FREECAD ASSEMBLY — COMPONENT RECIPES ("Machine")

This assembly document has 15 components, labeled P0..P14 below (a component is one placed body or linked part). 12 of them carry a construction recipe — the FreeCAD feature program that regenerates the part from scratch, quoted from this document or its linked companion documents; the rest are supplied as boundary geometry only. No exploded tour is included for this assembly.
COMPONENT P0 — recipe-attached ("Back Left Plate Frame", modeled in this document).
Construction recipe (the document's own serialized feature program — sketch geometry with constraints, then the solid features built on it; lengths are millimeters unless a unit is written):

FEATURE [PartDesign::FeatureBase] Clone
  BaseFeature = -> Body002
  Placement = pos=(0,0,0) rot=(0,0,1;3.14159rad)
FEATURE [PartDesign::Body] Body  label="Back Left Plate Frame"
  BaseFeature = -> Body002
  Group = -> [Clone]
  Origin = -> Origin
  Placement = pos=(20,508,0) rot=(0,0,1;0rad)
  Tip = -> Clone
  expr: .Placement.Base.x = 20
COMPONENT P1 — recipe-attached ("Front Left Plate Frame", modeled in this document).
Construction recipe (the document's own serialized feature program — sketch geometry with constraints, then the solid features built on it; lengths are millimeters unless a unit is written):

FEATURE [Sketcher::SketchObject] Sketch003
  FullyConstrained = false
  MapMode = 5
  Placement = pos=(0,0,0) rot=(1,0,0;1.5708rad)
  Support = -> [XZ_Plane002]
  expr: Constraints[11] = Spreadsheet.machine_heigh
  expr: Constraints[34] = 25 + Spreadsheet.rail_wheel_outer_clearing
  expr: Constraints[35] = 25 + Spreadsheet.rail_wheel_outer_clearing
  sketch-geometry (15):
    g0: LineSegment StartX=-20 StartY=140 StartZ=0 EndX=26 EndY=140 EndZ=0
    g1: LineSegment StartX=26 StartY=140 StartZ=0 EndX=26 EndY=0 EndZ=0
    g2: LineSegment StartX=26 StartY=0 StartZ=0 EndX=-20 EndY=0 EndZ=0
    g3: LineSegment StartX=-20 StartY=0 StartZ=0 EndX=-20 EndY=140 EndZ=0
    g4: GeomPoint X=0 Y=0 Z=0
    g5: LineSegment StartX=3.41 StartY=104.4 StartZ=0 EndX=11.59 EndY=104.4 EndZ=0
    g6: LineSegment StartX=13.5 StartY=102.49 StartZ=0 EndX=13.5 EndY=101.04 EndZ=0
    g7: LineSegment StartX=11.59 StartY=99.13 StartZ=0 EndX=3.41 EndY=99.13 EndZ=0
    g8: LineSegment StartX=1.5 StartY=101.04 StartZ=0 EndX=1.5 EndY=102.49 EndZ=0
    g9: ArcOfCircle CenterX=3.41 CenterY=102.49 CenterZ=0 NormalX=0 NormalY=0 NormalZ=1 AngleXU=0 Radius=1.91 StartAngle=1.5708 EndAngle=3.14159
    g10: ArcOfCircle CenterX=3.41 CenterY=101.04 CenterZ=0 NormalX=0 NormalY=0 NormalZ=1 AngleXU=0 Radius=1.91 StartAngle=3.14159 EndAngle=4.71239
    g11: ArcOfCircle CenterX=11.59 CenterY=102.49 CenterZ=0 NormalX=0 NormalY=0 NormalZ=1 AngleXU=0 Radius=1.91 StartAngle=1e-16 EndAngle=1.5708
    g12: ArcOfCircle CenterX=11.59 CenterY=101.04 CenterZ=0 NormalX=0 NormalY=0 NormalZ=1 AngleXU=0 Radius=1.91 StartAngle=4.71239 EndAngle=6.28319
    g13: GeomPoint X=7.5 Y=99.13 Z=0
    g14: Circle CenterX=7.5 CenterY=120 CenterZ=0 NormalX=0 NormalY=0 NormalZ=1 AngleXU=0 Radius=4.20728
  constraints (36):
    c: Coincident(g0,g1)
    c: Coincident(g1,g2)
    c: Coincident(g2,g3)
    c: Coincident(g3,g0)
    c: Horizontal(g0)
    c: Horizontal(g2)
    c: Vertical(g1)
    c: Vertical(g3)
    c: DistanceX(g2,g2) = 46
    c: Horizontal(g4,g-1)
    c: Vertical(g4,g-1)
    c: DistanceY(g1,g1) = 140
    c: Horizontal(g5)
    c: Horizontal(g7)
    c: Vertical(g6)
    c: Vertical(g8)
    c: Tangent(g5,g9) = 1.5708
    c: Tangent(g8,g9) = 1.5708
    c: Tangent(g7,g10) = 1.5708
    c: Tangent(g8,g10) = 1.5708
    c: Tangent(g5,g11) = 1.5708
    c: Tangent(g6,g11) = 1.5708
    c: Tangent(g6,g12) = 1.5708
    c: Tangent(g7,g12) = 1.5708
    c: DistanceX(g8,g6) = 12
    c: Symmetric(g7,g7,g13)
    c: Equal(g12,g11)
    c: Equal(g11,g9)
    c: Equal(g9,g10)
    c: DistanceY(g14,g0) = 20
    c: DistanceY(g5,g14) = 15.6
    c: DistanceY(g7,g5) = 5.27
    c: DistanceY(g8,g8) = 1.45
    c: Block(g3)
    c: DistanceX(g0,g14) = 27.5
    c: DistanceX(g0,g13) = 27.5
FEATURE [PartDesign::Pad] Pad001  label="Frame Plate Body"
  Direction = (1,1,1)
  Length = 8
  Length2 = 100
  Placement = pos=(0,0,0) rot=(1,0,0;1.5708rad)
  Profile = -> Sketch003
  Reversed = true
  Type = 0
FEATURE [Sketcher::SketchObject] Sketch004
  ExternalGeometry = -> [Pad001,Sketch003]
  FullyConstrained = true
  MapMode = 5
  Placement = pos=(0,0,0) rot=(1,0,0;1.5708rad)
  Support = -> [XZ_Plane002]
  expr: Constraints[19] = Spreadsheet.machine_heigh - Spreadsheet.board_heigh_from_top - 35.1
  expr: Constraints[22] = Spreadsheet.machine_heigh - Spreadsheet.bed_support_height + 20
  expr: Constraints[26] = 25 + Spreadsheet.rail_wheel_outer_clearing
  sketch-geometry (10):
    g0: Circle CenterX=-10 CenterY=10 CenterZ=0 NormalX=0 NormalY=0 NormalZ=1 AngleXU=0 Radius=2.5
    g1: Circle CenterX=10 CenterY=10 CenterZ=0 NormalX=0 NormalY=0 NormalZ=1 AngleXU=0 Radius=2.5
    g2: LineSegment StartX=-10 StartY=10 StartZ=0 EndX=10 EndY=10 EndZ=0
    g3: GeomPoint X=0 Y=10 Z=0
    g4: Circle CenterX=7.5 CenterY=130 CenterZ=0 NormalX=0 NormalY=0 NormalZ=1 AngleXU=0 Radius=2.5
    g5: Circle CenterX=7.5 CenterY=110 CenterZ=0 NormalX=0 NormalY=0 NormalZ=1 AngleXU=0 Radius=2.5
    g6: Circle CenterX=-10 CenterY=44.9 CenterZ=0 NormalX=0 NormalY=0 NormalZ=1 AngleXU=0 Radius=2.5
    g7: Circle CenterX=10 CenterY=44.9 CenterZ=0 NormalX=0 NormalY=0 NormalZ=1 AngleXU=0 Radius=2.5
    g8: Circle CenterX=-10 CenterY=60.9 CenterZ=0 NormalX=0 NormalY=0 NormalZ=1 AngleXU=0 Radius=2.5
    g9: Circle CenterX=10 CenterY=60.9 CenterZ=0 NormalX=0 NormalY=0 NormalZ=1 AngleXU=0 Radius=2.5
  constraints (27):
    c: Radius(g0) = 2.5
    c: Equal(g0,g1)
    c: Horizontal(g0,g1)
    c: DistanceX(g0,g1) = 20
    c: Coincident(g2,g0)
    c: Coincident(g2,g1)
    c: Symmetric(g2,g2,g3)
    c: Vertical(g3,g-1)
    c: DistanceY(g-1,g3) = 10
    c: Vertical(g5,g4)
    c: Equal(g5,g4)
    c: Equal(g4,g1)
    c: DistanceY(g5,g4) = 20
    c: DistanceY(g4,g-5) = 10
    c: Equal(g6,g7)
    c: Equal(g7,g0)
    c: Vertical(g6,g0)
    c: Vertical(g7,g1)
    c: Horizontal(g6,g7)
    c: DistanceY(g-4,g6) = 44.9
    c: Equal(g8,g9)
    c: Equal(g9,g6)
    c: DistanceY(g-1,g8) = 60.9
    c: Horizontal(g8,g9)
    c: Vertical(g6,g8)
    c: Vertical(g7,g9)
    c: DistanceX(g-3,g4) = 27.5
FEATURE [PartDesign::Hole] Hole  label="Frame Plate Mount Holes 1"
  BaseFeature = -> Pad001
  Depth = 25
  DepthType = 0
  Diameter = 5.5
  DrillForDepth = false
  DrillPoint = 0
  DrillPointAngle = 118
  HoleCutCountersinkAngle = 90
  HoleCutCustomValues = false
  HoleCutDepth = 5.4
  HoleCutDiameter = 9.2
  HoleCutType = 0
  ModelActualThread = false
  Placement = pos=(0,0,0) rot=(1,0,0;1.5708rad)
  Profile = -> Sketch004
  Tapered = false
  TaperedAngle = 90
  ThreadAngle = 0
  ThreadClass = 0
  ThreadCutOffInner = 0
  ThreadCutOffOuter = 0
  ThreadDirection = 0
  ThreadFit = 0
  ThreadPitch = 0
  ThreadSize = 13
  ThreadType = 1
  Threaded = false
FEATURE [PartDesign::Body] Body002  label="Front Left Plate Frame"
  Group = -> [Sketch003,Pad001,Sketch004,Hole]
  Origin = -> Origin002
  Placement = pos=(20,0,0) rot=(0,0,1;3.14159rad)
  Tip = -> Hole
  expr: .Placement.Base.x = 20
COMPONENT P2 — recipe-attached ("Front Right Plate Frame", modeled in this document).
Construction recipe (the document's own serialized feature program — sketch geometry with constraints, then the solid features built on it; lengths are millimeters unless a unit is written):

FEATURE [PartDesign::FeatureBase] Clone001
  BaseFeature = -> Body002
  Placement = pos=(0,0,0) rot=(0,0,1;3.14159rad)
FEATURE [PartDesign::Body] Body003  label="Front Right Plate Frame"
  BaseFeature = -> Body002
  Group = -> [Clone001]
  Origin = -> Origin003
  Placement = pos=(980,-8,0) rot=(0,0,1;3.14159rad)
  Tip = -> Clone001
  expr: .Placement.Base.x = Spreadsheet.machine_length - 20
COMPONENT P3 — recipe-attached ("Back Right Plate Frame", modeled in this document).
Construction recipe (the document's own serialized feature program — sketch geometry with constraints, then the solid features built on it; lengths are millimeters unless a unit is written):

FEATURE [PartDesign::FeatureBase] Clone002
  BaseFeature = -> Body002
  Placement = pos=(0,0,0) rot=(0,0,1;3.14159rad)
FEATURE [PartDesign::Body] Body004  label="Back Right Plate Frame"
  BaseFeature = -> Body002
  Group = -> [Clone002]
  Origin = -> Origin004
  Placement = pos=(980,500,0) rot=(0,0,1;3.14159rad)
  Tip = -> Clone002
  expr: .Placement.Base.x = Spreadsheet.machine_length - 20
COMPONENT P4 — recipe-attached ("Bed", modeled in this document).
Construction recipe (the document's own serialized feature program — sketch geometry with constraints, then the solid features built on it; lengths are millimeters unless a unit is written):

FEATURE [Sketcher::SketchObject] Sketch005
  FullyConstrained = true
  MapMode = 5
  Support = -> [XY_Plane005]
  expr: Constraints[9] = Spreadsheet.machine_width
  expr: Constraints[10] = Spreadsheet.machine_length
  sketch-geometry (4):
    g0: LineSegment StartX=0 StartY=500 StartZ=0 EndX=1000 EndY=500 EndZ=0
    g1: LineSegment StartX=1000 StartY=500 StartZ=0 EndX=1000 EndY=180 EndZ=0
    g2: LineSegment StartX=1000 StartY=180 StartZ=0 EndX=0 EndY=180 EndZ=0
    g3: LineSegment StartX=0 StartY=180 StartZ=0 EndX=0 EndY=500 EndZ=0
  constraints (12):
    c: Coincident(g0,g1)
    c: Coincident(g1,g2)
    c: Coincident(g2,g3)
    c: Coincident(g3,g0)
    c: Horizontal(g0)
    c: Horizontal(g2)
    c: Vertical(g1)
    c: Vertical(g3)
    c: Vertical(g2,g-1)
    c: DistanceY(g-1,g0) = 500
    c: DistanceX(g0,g0) = 1000
    c: DistanceY(g3,g3) = 320
FEATURE [PartDesign::Pad] Pad
  Direction = (1,1,1)
  Length = 20
  Length2 = 100
  Profile = -> Sketch005
  Type = 0
  expr: Length = Spreadsheet.bed_thickness
FEATURE [PartDesign::Body] Body005  label="Bed"
  Group = -> [Sketch005,Pad]
  Origin = -> Origin005
  Placement = pos=(0,0,50.9) rot=(0,0,1;0rad)
  Tip = -> Pad
  expr: .Placement.Base.z = Spreadsheet.machine_heigh - Spreadsheet.bed_support_height + 10
COMPONENT P5 — recipe-attached ("Left Side Cover", modeled in this document).
Construction recipe (the document's own serialized feature program — sketch geometry with constraints, then the solid features built on it; lengths are millimeters unless a unit is written):

FEATURE [Sketcher::SketchObject] Sketch015
  FullyConstrained = true
  MapMode = 5
  Placement = pos=(0,0,0) rot=(0.57735,0.57735,0.57735;2.0944rad)
  Support = -> [YZ_Plane013]
  expr: Constraints[20] = Spreadsheet.machine_heigh - Spreadsheet.bed_support_height + 30
  expr: Constraints[7] = Spreadsheet.machine_width
  sketch-geometry (7):
    g0: LineSegment StartX=500 StartY=70.9 StartZ=0 EndX=500 EndY=0 EndZ=0
    g1: LineSegment StartX=500 StartY=0 StartZ=0 EndX=0 EndY=0 EndZ=0
    g2: LineSegment StartX=0 StartY=0 StartZ=0 EndX=0 EndY=54.9 EndZ=0
    g3: LineSegment StartX=0 StartY=54.9 StartZ=0 EndX=175 EndY=54.9 EndZ=0
    g4: LineSegment StartX=180 StartY=59.9 StartZ=0 EndX=180 EndY=70.9 EndZ=0
    g5: LineSegment StartX=180 StartY=70.9 StartZ=0 EndX=500 EndY=70.9 EndZ=0
    g6: ArcOfCircle CenterX=175 CenterY=59.9 CenterZ=0 NormalX=0 NormalY=0 NormalZ=1 AngleXU=0 Radius=5 StartAngle=4.71239 EndAngle=6.28319
  constraints (24):
    c: Coincident(g0,g1)
    c: Coincident(g1,g2)
    c: Horizontal(g1)
    c: Vertical(g0)
    c: Vertical(g2)
    c: Horizontal(g1,g-1)
    c: Vertical(g1,g-1)
    c: DistanceX(g1,g1) = 500
    c: Horizontal(g3)
    c: Vertical(g3,g2)
    c: Block(g2)
    c: Horizontal(g3,g2)
    c: Vertical(g4)
    c: Horizontal(g5)
    c: Horizontal(g5,g4)
    c: Vertical(g5,g4)
    c: Vertical(g0,g5)
    c: DistanceX(g5,g5) = 320
    c: Block(g5)
    c: Horizontal(g0,g5)
    c: DistanceY(g0,g0) = 70.9
    c: Tangent(g3,g6) = -1.5708
    c: Tangent(g4,g6) = -1.5708
    c: Radius(g6) = 5
FEATURE [PartDesign::Pad] Pad004
  Direction = (1,1,1)
  Length = 6
  Length2 = 100
  Placement = pos=(0,0,0) rot=(0.57735,0.57735,0.57735;2.0944rad)
  Profile = -> Sketch015
  Reversed = true
  Type = 0
FEATURE [Sketcher::SketchObject] Sketch016
  ExternalGeometry = -> [Sketch015]
  FullyConstrained = false
  MapMode = 5
  Placement = pos=(0,0,0) rot=(0.57735,0.57735,0.57735;2.0944rad)
  Support = -> [YZ_Plane013]
  expr: Constraints[13] = Spreadsheet.machine_heigh - Spreadsheet.bed_support_height + 20
  expr: Constraints[10] = Spreadsheet.machine_heigh - Spreadsheet.board_heigh_from_top - 35.1
  sketch-geometry (42):
    g0: Circle CenterX=10 CenterY=44.9 CenterZ=0 NormalX=0 NormalY=0 NormalZ=1 AngleXU=0 Radius=2.5
    g1: Circle CenterX=10 CenterY=10 CenterZ=0 NormalX=0 NormalY=0 NormalZ=1 AngleXU=0 Radius=2.5
    g2: Circle CenterX=70 CenterY=44.9 CenterZ=0 NormalX=0 NormalY=0 NormalZ=1 AngleXU=0 Radius=2.5
    g3: Circle CenterX=70 CenterY=10 CenterZ=0 NormalX=0 NormalY=0 NormalZ=1 AngleXU=0 Radius=2.5
    g4: Circle CenterX=190 CenterY=60.9 CenterZ=0 NormalX=0 NormalY=0 NormalZ=1 AngleXU=0 Radius=2.5
    g5: Circle CenterX=210 CenterY=60.9 CenterZ=0 NormalX=0 NormalY=0 NormalZ=1 AngleXU=0 Radius=2.5
    g6: Circle CenterX=230 CenterY=60.9 CenterZ=0 NormalX=0 NormalY=0 NormalZ=1 AngleXU=0 Radius=2.5
    g7: LineSegment StartX=210 StartY=60.9 StartZ=0 EndX=230 EndY=60.9 EndZ=0
    g8: Circle CenterX=250 CenterY=60.9 CenterZ=0 NormalX=0 NormalY=0 NormalZ=1 AngleXU=0 Radius=2.5
    g9: LineSegment StartX=230 StartY=60.9 StartZ=0 EndX=250 EndY=60.9 EndZ=0
    g10: Circle CenterX=270 CenterY=60.9 CenterZ=0 NormalX=0 NormalY=0 NormalZ=1 AngleXU=0 Radius=2.5
    g11: LineSegment StartX=250 StartY=60.9 StartZ=0 EndX=270 EndY=60.9 EndZ=0
    g12: Circle CenterX=290 CenterY=60.9 CenterZ=0 NormalX=0 NormalY=0 NormalZ=1 AngleXU=0 Radius=2.5
    g13: LineSegment StartX=270 StartY=60.9 StartZ=0 EndX=290 EndY=60.9 EndZ=0
    g14: Circle CenterX=310 CenterY=60.9 CenterZ=0 NormalX=0 NormalY=0 NormalZ=1 AngleXU=0 Radius=2.5
    g15: LineSegment StartX=290 StartY=60.9 StartZ=0 EndX=310 EndY=60.9 EndZ=0
    g16: Circle CenterX=330 CenterY=60.9 CenterZ=0 NormalX=0 NormalY=0 NormalZ=1 AngleXU=0 Radius=2.5
    g17: LineSegment StartX=310 StartY=60.9 StartZ=0 EndX=330 EndY=60.9 EndZ=0
    g18: Circle CenterX=350 CenterY=60.9 CenterZ=0 NormalX=0 NormalY=0 NormalZ=1 AngleXU=0 Radius=2.5
    g19: LineSegment StartX=330 StartY=60.9 StartZ=0 EndX=350 EndY=60.9 EndZ=0
    g20: Circle CenterX=370 CenterY=60.9 CenterZ=0 NormalX=0 NormalY=0 NormalZ=1 AngleXU=0 Radius=2.5
    g21: LineSegment StartX=350 StartY=60.9 StartZ=0 EndX=370 EndY=60.9 EndZ=0
    g22: Circle CenterX=390 CenterY=60.9 CenterZ=0 NormalX=0 NormalY=0 NormalZ=1 AngleXU=0 Radius=2.5
    g23: LineSegment StartX=370 StartY=60.9 StartZ=0 EndX=390 EndY=60.9 EndZ=0
    g24: Circle CenterX=410 CenterY=60.9 CenterZ=0 NormalX=0 NormalY=0 NormalZ=1 AngleXU=0 Radius=2.5
    g25: LineSegment StartX=390 StartY=60.9 StartZ=0 EndX=410 EndY=60.9 EndZ=0
    g26: Circle CenterX=430 CenterY=60.9 CenterZ=0 NormalX=0 NormalY=0 NormalZ=1 AngleXU=0 Radius=2.5
    g27: LineSegment StartX=410 StartY=60.9 StartZ=0 EndX=430 EndY=60.9 EndZ=0
    g28: Circle CenterX=450 CenterY=60.9 CenterZ=0 NormalX=0 NormalY=0 NormalZ=1 AngleXU=0 Radius=2.5
    g29: LineSegment StartX=430 StartY=60.9 StartZ=0 EndX=450 EndY=60.9 EndZ=0
    g30: Circle CenterX=470 CenterY=60.9 CenterZ=0 NormalX=0 NormalY=0 NormalZ=1 AngleXU=0 Radius=2.5
    g31: LineSegment StartX=450 StartY=60.9 StartZ=0 EndX=470 EndY=60.9 EndZ=0
    g32: Circle CenterX=490 CenterY=60.9 CenterZ=0 NormalX=0 NormalY=0 NormalZ=1 AngleXU=0 Radius=2.5
    g33: LineSegment StartX=470 StartY=60.9 StartZ=0 EndX=490 EndY=60.9 EndZ=0
    g34: Circle CenterX=170 CenterY=10 CenterZ=0 NormalX=0 NormalY=0 NormalZ=1 AngleXU=0 Radius=2.5
    g35: Circle CenterX=250 CenterY=10 CenterZ=0 NormalX=0 NormalY=0 NormalZ=1 AngleXU=0 Radius=2.5
    g36: Circle CenterX=330 CenterY=10 CenterZ=0 NormalX=0 NormalY=0 NormalZ=1 AngleXU=0 Radius=2.5
    g37: Circle CenterX=410 CenterY=10 CenterZ=0 NormalX=0 NormalY=0 NormalZ=1 AngleXU=0 Radius=2.5
    g38: Circle CenterX=490 CenterY=10 CenterZ=0 NormalX=0 NormalY=0 NormalZ=1 AngleXU=0 Radius=2.5
    g39: Circle CenterX=120 CenterY=10 CenterZ=0 NormalX=0 NormalY=0 NormalZ=1 AngleXU=0 Radius=2.5
    g40: LineSegment StartX=70 StartY=10 StartZ=0 EndX=170 EndY=10 EndZ=0
    g41: GeomPoint X=120 Y=10 Z=0
  constraints (94):
    c: Radius(g0) = 2.5
    c: Equal(g0,g2)
    c: Equal(g2,g3)
    c: Equal(g3,g1)
    c: Horizontal(g0,g2)
    c: Horizontal(g1,g3)
    c: Vertical(g0,g1)
    c: DistanceX(g0,g2) = 60
    c: Vertical(g2,g3)
    c: DistanceX(g-1,g1) = 10
    c: DistanceY(g-1,g0) = 44.9
    c: DistanceY(g-1,g1) = 10
    c: Equal(g0,g4)
    c: DistanceY(g-1,g4) = 60.9
    c: DistanceX(g-3,g4) = 10
    c: Equal(g4,g5)
    c: Coincident(g5,g7)
    c: Coincident(g6,g7)
    c: Distance(g7) = 20
    c: Angle(g7) = 0
    c: Coincident(g6,g9)
    c: Coincident(g8,g9)
    c: Equal(g7,g9)
    c: Parallel(g9,g7)
    c: Coincident(g8,g11)
    c: Coincident(g10,g11)
    c: Equal(g7,g11)
    c: Parallel(g11,g7)
    c: Coincident(g10,g13)
    c: Coincident(g12,g13)
    c: Equal(g7,g13)
    c: Parallel(g13,g7)
    c: Coincident(g12,g15)
    c: Coincident(g14,g15)
    c: Equal(g7,g15)
    c: Parallel(g15,g7)
    c: Coincident(g14,g17)
    c: Coincident(g16,g17)
    c: Equal(g7,g17)
    c: Parallel(g17,g7)
    c: Coincident(g16,g19)
    c: Coincident(g18,g19)
    c: Equal(g7,g19)
    c: Parallel(g19,g7)
    c: Coincident(g18,g21)
    c: Coincident(g20,g21)
    c: Equal(g7,g21)
    c: Parallel(g21,g7)
    c: Coincident(g20,g23)
    c: Coincident(g22,g23)
    c: Equal(g7,g23)
    c: Parallel(g23,g7)
    c: Coincident(g22,g25)
    c: Coincident(g24,g25)
    c: Equal(g7,g25)
    c: Parallel(g25,g7)
    c: Coincident(g24,g27)
    c: Coincident(g26,g27)
    c: Equal(g7,g27)
    c: Parallel(g27,g7)
    c: Coincident(g26,g29)
    c: Coincident(g28,g29)
    c: Equal(g7,g29)
    c: Parallel(g29,g7)
    c: Coincident(g28,g31)
    c: Coincident(g30,g31)
    c: Equal(g7,g31)
    c: Parallel(g31,g7)
    c: Coincident(g30,g33)
    c: Coincident(g32,g33)
    c: Equal(g7,g33)
    c: Parallel(g33,g7)
    c: Horizontal(g5,g4)
    c: DistanceX(g4,g5) = 20
    c: Equal(g34,g35)
    c: Equal(g35,g36)
    c: Equal(g36,g37)
    c: Equal(g37,g38)
    c: Equal(g38,g4)
    c: Horizontal(g34,g35)
    c: Horizontal(g35,g36)
    c: Horizontal(g36,g37)
    c: Horizontal(g37,g38)
    c: Vertical(g38,g32)
    c: Vertical(g16,g36)
    c: Vertical(g8,g35)
    c: Vertical(g24,g37)
    c: DistanceY(g-1,g34) = 10
    c: Equal(g39,g4)
    c: DistanceX(g34,g35) = 80
    c: Coincident(g40,g3)
    c: Coincident(g40,g34)
    c: Symmetric(g40,g40,g41)
    c: Coincident(g39,g41)
FEATURE [PartDesign::Hole] Hole005
  BaseFeature = -> Pad004
  Depth = 25
  DepthType = 0
  Diameter = 5.5
  DrillForDepth = false
  DrillPoint = 1
  DrillPointAngle = 118
  HoleCutCountersinkAngle = 90
  HoleCutCustomValues = false
  HoleCutDepth = 0
  HoleCutDiameter = 6.1
  HoleCutType = 0
  ModelActualThread = false
  Placement = pos=(0,0,0) rot=(0.57735,0.57735,0.57735;2.0944rad)
  Profile = -> Sketch016
  Tapered = false
  TaperedAngle = 90
  ThreadAngle = 0
  ThreadClass = 0
  ThreadCutOffInner = 0
  ThreadCutOffOuter = 0
  ThreadDirection = 0
  ThreadFit = 0
  ThreadPitch = 0
  ThreadSize = 13
  ThreadType = 1
  Threaded = false
FEATURE [PartDesign::Body] Body009  label="Left Side Cover"
  Group = -> [Sketch015,Pad004,Sketch016,Hole005]
  Origin = -> Origin013
  Tip = -> Hole005
COMPONENT P6 — recipe-attached ("Right Side Cover", modeled in this document).
Construction recipe (the document's own serialized feature program — sketch geometry with constraints, then the solid features built on it; lengths are millimeters unless a unit is written):

FEATURE [PartDesign::FeatureBase] Clone003
  BaseFeature = -> Body009
FEATURE [PartDesign::Body] Body010  label="Right Side Cover"
  BaseFeature = -> Body009
  Group = -> [Clone003]
  Origin = -> Origin014
  Placement = pos=(1006,0,0) rot=(0,0,1;0rad)
  Tip = -> Clone003
  expr: .Placement.Base.x = Spreadsheet.machine_length + 6
COMPONENT P7 — recipe-attached ("X-Axis Plate", modeled in this document).
Construction recipe (the document's own serialized feature program — sketch geometry with constraints, then the solid features built on it; lengths are millimeters unless a unit is written):

FEATURE [Sketcher::SketchObject] Sketch  label="y-plate-body"
  FullyConstrained = false
  MapMode = 5
  Support = -> [XY_Plane016]
  sketch-geometry (13):
    g0: LineSegment StartX=-53.5834 StartY=-36.7445 StartZ=0 EndX=-53.5834 EndY=3.25546 EndZ=0
    g1: LineSegment StartX=-53.5834 StartY=3.25546 StartZ=0 EndX=-13.5834 EndY=3.25546 EndZ=0
    g2: LineSegment StartX=-10.5834 StartY=6.25546 StartZ=0 EndX=-10.5834 EndY=27.0662 EndZ=0
    g3: LineSegment StartX=-7.5834 StartY=30.0662 StartZ=0 EndX=70.0566 EndY=30.0662 EndZ=0
    g4: LineSegment StartX=70.0566 StartY=30.0662 StartZ=0 EndX=70.0566 EndY=-97.5802 EndZ=0
    g5: LineSegment StartX=67.0566 StartY=-100.58 StartZ=0 EndX=-7.5834 EndY=-100.58 EndZ=0
    g6: LineSegment StartX=-10.5834 StartY=-97.5802 StartZ=0 EndX=-10.5834 EndY=-39.7445 EndZ=0
    g7: LineSegment StartX=-13.5834 StartY=-36.7445 StartZ=0 EndX=-53.5834 EndY=-36.7445 EndZ=0
    g8: ArcOfCircle CenterX=-13.5834 CenterY=-39.7445 CenterZ=0 NormalX=0 NormalY=0 NormalZ=1 AngleXU=0 Radius=3 StartAngle=1e-15 EndAngle=1.5708
    g9: ArcOfCircle CenterX=-13.5834 CenterY=6.25546 CenterZ=0 NormalX=0 NormalY=0 NormalZ=1 AngleXU=0 Radius=3 StartAngle=4.71239 EndAngle=6.28319
    g10: ArcOfCircle CenterX=-7.5834 CenterY=27.0662 CenterZ=0 NormalX=0 NormalY=0 NormalZ=1 AngleXU=0 Radius=3 StartAngle=1.5708 EndAngle=3.14159
    g11: ArcOfCircle CenterX=67.0566 CenterY=-97.5802 CenterZ=0 NormalX=0 NormalY=0 NormalZ=1 AngleXU=0 Radius=3 StartAngle=4.71239 EndAngle=6.28319
    g12: ArcOfCircle CenterX=-7.5834 CenterY=-97.5802 CenterZ=0 NormalX=0 NormalY=0 NormalZ=1 AngleXU=0 Radius=3 StartAngle=3.14159 EndAngle=4.71239
  constraints (32):
    c: Horizontal(g1)
    c: Vertical(g2)
    c: Horizontal(g3)
    c: Vertical(g4)
    c: Horizontal(g5)
    c: Vertical(g6)
    c: Horizontal(g7)
    c: Tangent(g6,g8) = -1.5708
    c: Tangent(g7,g8) = -1.5708
    c: Tangent(g1,g9) = -1.5708
    c: Tangent(g2,g9) = -1.5708
    c: Tangent(g2,g10) = 1.5708
    c: Tangent(g3,g10) = 1.5708
    c: Tangent(g4,g11) = 1.5708
    c: Tangent(g5,g11) = 1.5708
    c: Tangent(g5,g12) = 1.5708
    c: Tangent(g6,g12) = 1.5708
    c: Radius(g12) = 3
    c: Equal(g12,g11)
    c: Equal(g10,g9)
    c: DistanceY(g7,g1) = 40
    c: Equal(g1,g7)
    c: DistanceX(g6,g4) = 80.64
    c: Horizontal(g0,g1)
    c: Vertical(g1,g0)
    c: Horizontal(g0,g7)
    c: Vertical(g0)
    c: Block(g0)
    c: Vertical(g7,g0)
    c: Equal(g8,g9)
    c: DistanceX(g1,g1) = 40
    c: Coincident(g3,g4)
FEATURE [PartDesign::Pad] Pad005
  Direction = (1,1,1)
  Length = 6
  Length2 = 100
  Profile = -> Sketch
  Type = 0
FEATURE [Sketcher::SketchObject] Sketch025  label="y-plate-x-axis-mount-threaded-holes"
  ExternalGeometry = -> [Sketch]
  FullyConstrained = true
  MapMode = 5
  Placement = pos=(0,0,6) rot=(0,0,1;0rad)
  Support = -> [Pad005]
  sketch-geometry (5):
    g0: Circle CenterX=-43.5834 CenterY=-6.74454 CenterZ=0 NormalX=0 NormalY=0 NormalZ=1 AngleXU=0 Radius=2.55
    g1: Circle CenterX=-43.5834 CenterY=-26.7445 CenterZ=0 NormalX=0 NormalY=0 NormalZ=1 AngleXU=0 Radius=2.55
    g2: LineSegment StartX=-43.5834 StartY=-6.74454 StartZ=0 EndX=-43.5834 EndY=-26.7445 EndZ=0
    g3: GeomPoint X=-43.5834 Y=-16.7445 Z=0
    g4: GeomPoint X=-53.5834 Y=-16.7445 Z=0
  constraints (10):
    c: Radius(g0) = 2.55
    c: Equal(g0,g1)
    c: Vertical(g1,g0)
    c: DistanceY(g1,g0) = 20
    c: Coincident(g2,g0)
    c: Coincident(g2,g1)
    c: DistanceX(g-3,g1) = 10
    c: Symmetric(g2,g2,g3)
    c: Symmetric(g-4,g-4,g4)
    c: Horizontal(g4,g3)
FEATURE [PartDesign::Hole] Hole006  label="ho-y-plate-x-axis-mount-threaded-holes"
  BaseFeature = -> Pad005
  Depth = 25
  DepthType = 0
  Diameter = 4.2
  DrillForDepth = false
  DrillPoint = 1
  DrillPointAngle = 118
  HoleCutCountersinkAngle = 90
  HoleCutCustomValues = false
  HoleCutDepth = 0
  HoleCutDiameter = 6.1
  HoleCutType = 0
  ModelActualThread = false
  Profile = -> Sketch025
  Tapered = false
  TaperedAngle = 90
  ThreadAngle = 60
  ThreadClass = 0
  ThreadCutOffInner = 0.0866025
  ThreadCutOffOuter = 0.173205
  ThreadDirection = 0
  ThreadFit = 1
  ThreadPitch = 0.8
  ThreadSize = 13
  ThreadType = 1
  Threaded = true
FEATURE [Sketcher::SketchObject] Sketch026  label="y-plate-wheel-excentric-holes"
  ExternalGeometry = -> [Sketch025,Sketch]
  FullyConstrained = true
  MapMode = 5
  Placement = pos=(0,0,6) rot=(0,0,1;0rad)
  Support = -> [Hole006]
  sketch-geometry (2):
    g0: Circle CenterX=-0.583397 CenterY=-31.8945 CenterZ=0 NormalX=0 NormalY=0 NormalZ=1 AngleXU=0 Radius=2.55
    g1: Circle CenterX=60.0566 CenterY=-31.8945 CenterZ=0 NormalX=0 NormalY=0 NormalZ=1 AngleXU=0 Radius=2.55
  constraints (6):
    c: Horizontal(g0,g1)
    c: DistanceX(g0,g1) = 60.64
    c: DistanceY(g0,g-3) = 5.15
    c: DistanceX(g-4,g0) = 10
    c: Radius(g0) = 2.55
    c: Equal(g0,g1)
FEATURE [PartDesign::Hole] Hole007
  BaseFeature = -> Hole006
  Depth = 25
  DepthType = 0
  Diameter = 7.2
  DrillForDepth = false
  DrillPoint = 1
  DrillPointAngle = 118
  HoleCutCountersinkAngle = 90
  HoleCutCustomValues = false
  HoleCutDepth = 0
  HoleCutDiameter = 0
  HoleCutType = 0
  ModelActualThread = false
  Profile = -> Sketch026
  Tapered = false
  TaperedAngle = 90
  ThreadAngle = 0
  ThreadClass = 0
  ThreadCutOffInner = 0
  ThreadCutOffOuter = 0
  ThreadDirection = 0
  ThreadFit = 1
  ThreadPitch = 0
  ThreadSize = 0
  ThreadType = 0
  Threaded = false
FEATURE [Sketcher::SketchObject] Sketch027  label="y-plate-wheel-holes"
  ExternalGeometry = -> [Sketch026]
  FullyConstrained = true
  MapMode = 5
  Placement = pos=(0,0,6) rot=(0,0,1;0rad)
  Support = -> [Hole007]
  sketch-geometry (2):
    g0: Circle CenterX=-0.583397 CenterY=-91.8945 CenterZ=0 NormalX=0 NormalY=0 NormalZ=1 AngleXU=0 Radius=3.6
    g1: Circle CenterX=60.0566 CenterY=-91.8945 CenterZ=0 NormalX=0 NormalY=0 NormalZ=1 AngleXU=0 Radius=3.6
  constraints (6):
    c: Radius(g0) = 3.6
    c: Equal(g0,g1)
    c: Horizontal(g0,g1)
    c: Vertical(g0,g-3)
    c: Vertical(g1,g-4)
    c: DistanceY(g0,g-3) = 60
FEATURE [PartDesign::Hole] Hole008
  BaseFeature = -> Hole007
  Depth = 25
  DepthType = 0
  Diameter = 5.3
  DrillForDepth = false
  DrillPoint = 1
  DrillPointAngle = 118
  HoleCutCountersinkAngle = 90
  HoleCutCustomValues = false
  HoleCutDepth = 0
  HoleCutDiameter = 0
  HoleCutType = 0
  ModelActualThread = false
  Profile = -> Sketch027
  Tapered = false
  TaperedAngle = 90
  ThreadAngle = 0
  ThreadClass = 0
  ThreadCutOffInner = 0
  ThreadCutOffOuter = 0
  ThreadDirection = 0
  ThreadFit = 1
  ThreadPitch = 0
  ThreadSize = 13
  ThreadType = 1
  Threaded = false
FEATURE [Sketcher::SketchObject] Sketch028  label="y-plate-nema-mount-holes"
  ExternalGeometry = -> [Sketch026]
  FullyConstrained = true
  MapMode = 5
  Placement = pos=(0,0,6) rot=(0,0,1;0rad)
  Support = -> [Hole008]
  sketch-geometry (8):
    g0: Circle CenterX=14.2366 CenterY=-0.39454 CenterZ=0 NormalX=0 NormalY=0 NormalZ=1 AngleXU=0 Radius=1.75
    g1: Circle CenterX=45.2366 CenterY=-0.39454 CenterZ=0 NormalX=0 NormalY=0 NormalZ=1 AngleXU=0 Radius=1.75
    g2: Circle CenterX=14.2366 CenterY=-31.3945 CenterZ=0 NormalX=0 NormalY=0 NormalZ=1 AngleXU=0 Radius=1.75
    g3: Circle CenterX=45.2366 CenterY=-31.3945 CenterZ=0 NormalX=0 NormalY=0 NormalZ=1 AngleXU=0 Radius=1.75
    g4: LineSegment StartX=14.2366 StartY=-0.39454 StartZ=0 EndX=45.2366 EndY=-31.3945 EndZ=0
    g5: GeomPoint X=29.7366 Y=-15.8945 Z=0
    g6: LineSegment StartX=-0.583397 StartY=-31.8945 StartZ=0 EndX=60.0566 EndY=-31.8945 EndZ=0
    g7: GeomPoint X=29.7366 Y=-31.8945 Z=0
  constraints (18):
    c: Horizontal(g0,g1)
    c: Horizontal(g2,g3)
    c: Vertical(g0,g2)
    c: Vertical(g1,g3)
    c: DistanceX(g0,g1) = 31
    c: DistanceY(g3,g1) = 31
    c: Radius(g0) = 1.75
    c: Equal(g0,g1)
    c: Equal(g1,g3)
    c: Equal(g3,g2)
    c: Coincident(g4,g0)
    c: Coincident(g4,g3)
    c: Symmetric(g4,g4,g5)
    c: Coincident(g6,g-3)
    c: Coincident(g6,g-4)
    c: Symmetric(g6,g6,g7)
    c: Vertical(g7,g5)
    c: DistanceY(g7,g5) = 16
FEATURE [PartDesign::Hole] Hole009
  BaseFeature = -> Hole008
  Depth = 25
  DepthType = 0
  Diameter = 3.2
  DrillForDepth = false
  DrillPoint = 1
  DrillPointAngle = 118
  HoleCutCountersinkAngle = 90
  HoleCutCustomValues = false
  HoleCutDepth = 0
  HoleCutDiameter = 6.1
  HoleCutType = 0
  ModelActualThread = false
  Profile = -> Sketch028
  Tapered = false
  TaperedAngle = 90
  ThreadAngle = 0
  ThreadClass = 0
  ThreadCutOffInner = 0
  ThreadCutOffOuter = 0
  ThreadDirection = 0
  ThreadFit = 1
  ThreadPitch = 0
  ThreadSize = 9
  ThreadType = 1
  Threaded = false
FEATURE [Sketcher::SketchObject] Sketch029  label="y-plate-nema-central-hole"
  ExternalGeometry = -> [Sketch028]
  FullyConstrained = true
  MapMode = 5
  Placement = pos=(0,0,6) rot=(0,0,1;0rad)
  Support = -> [Hole009]
  sketch-geometry (3):
    g0: Circle CenterX=29.7366 CenterY=-15.8945 CenterZ=0 NormalX=0 NormalY=0 NormalZ=1 AngleXU=0 Radius=12.5
    g1: LineSegment StartX=14.2366 StartY=-0.39454 StartZ=0 EndX=45.2366 EndY=-31.3945 EndZ=0
    g2: GeomPoint X=29.7366 Y=-15.8945 Z=0
  constraints (5):
    c: Radius(g0) = 12.5
    c: Coincident(g1,g-3)
    c: Coincident(g1,g-4)
    c: Symmetric(g1,g1,g2)
    c: Coincident(g2,g0)
FEATURE [PartDesign::Pocket] Pocket001
  BaseFeature = -> Hole009
  Length = 5
  Length2 = 100
  Profile = -> Sketch029
  Type = 1
FEATURE [PartDesign::Body] Body012  label="X-Axis Plate"
  Group = -> [Sketch,Sketch025,Sketch026,Pad005,Hole006,Hole007,Sketch027,Hole008,Sketch028,Sketch029,Hole009,Pocket001,Sketch030,Hole010,Sketch031,Hole011,Sketch032,Hole012,Sketch033,Pocket]
  Origin = -> Origin016
  Tip = -> Pocket
FEATURE [Sketcher::SketchObject] Sketch030  label="y-plate-drag-chain-support"
  ExternalGeometry = -> [Sketch]
  FullyConstrained = false
  MapMode = 5
  Placement = pos=(0,0,0) rot=(1,0,0;3.14159rad)
  Support = -> [Clone004]
  sketch-geometry (3):
    g0: Circle CenterX=40.0566 CenterY=-20.1055 CenterZ=0 NormalX=0 NormalY=0 NormalZ=1 AngleXU=0 Radius=2.5
    g1: Circle CenterX=60.0566 CenterY=-20.1055 CenterZ=0 NormalX=0 NormalY=0 NormalZ=1 AngleXU=0 Radius=2.5
    g2: LineSegment StartX=40.0566 StartY=-20.1055 StartZ=0 EndX=60.0566 EndY=-20.1055 EndZ=0
  constraints (7):
    c: Radius(g0) = 2.5
    c: Equal(g0,g1)
    c: Horizontal(g0,g1)
    c: DistanceX(g0,g1) = 20
    c: Coincident(g2,g0)
    c: Coincident(g2,g1)
    c: DistanceX(g1,g-3) = 10
FEATURE [PartDesign::Hole] Hole010
  BaseFeature = -> Pocket001
  Depth = 25
  DepthType = 0
  Diameter = 5.3
  DrillForDepth = false
  DrillPoint = 1
  DrillPointAngle = 118
  HoleCutCountersinkAngle = 90
  HoleCutCustomValues = false
  HoleCutDepth = 0
  HoleCutDiameter = 6.1
  HoleCutType = 0
  ModelActualThread = false
  Profile = -> Sketch030
  Tapered = false
  TaperedAngle = 90
  ThreadAngle = 0
  ThreadClass = 0
  ThreadCutOffInner = 0
  ThreadCutOffOuter = 0
  ThreadDirection = 0
  ThreadFit = 1
  ThreadPitch = 0
  ThreadSize = 13
  ThreadType = 1
  Threaded = false
FEATURE [Sketcher::SketchObject] Sketch031  label="y-plate-x-axis-mount-holes"
  ExternalGeometry = -> [Sketch025]
  FullyConstrained = true
  MapMode = 5
  Placement = pos=(0,0,6) rot=(0,0,1;0rad)
  Support = -> [Hole010]
  sketch-geometry (2):
    g0: Circle CenterX=-23.5834 CenterY=-6.74454 CenterZ=0 NormalX=0 NormalY=0 NormalZ=1 AngleXU=0 Radius=2.55
    g1: Circle CenterX=-23.5834 CenterY=-26.7445 CenterZ=0 NormalX=0 NormalY=0 NormalZ=1 AngleXU=0 Radius=2.55
  constraints (6):
    c: Equal(g1,g0)
    c: Equal(g0,g-4)
    c: Horizontal(g-3,g0)
    c: Horizontal(g-4,g1)
    c: Vertical(g1,g0)
    c: DistanceX(g-3,g0) = 20
FEATURE [PartDesign::Hole] Hole011  label="ho-y-plate-x-axis-mount-holes"
  BaseFeature = -> Hole010
  Depth = 25
  DepthType = 0
  Diameter = 5.3
  DrillForDepth = false
  DrillPoint = 1
  DrillPointAngle = 118
  HoleCutCountersinkAngle = 90
  HoleCutCustomValues = false
  HoleCutDepth = 0
  HoleCutDiameter = 6.1
  HoleCutType = 0
  ModelActualThread = false
  Profile = -> Sketch031
  Tapered = false
  TaperedAngle = 90
  ThreadAngle = 60
  ThreadClass = 0
  ThreadCutOffInner = 0.0866025
  ThreadCutOffOuter = 0.173205
  ThreadDirection = 1
  ThreadFit = 1
  ThreadPitch = 0.8
  ThreadSize = 13
  ThreadType = 1
  Threaded = false
FEATURE [Sketcher::SketchObject] Sketch032  label="y-plate-drag-mount-hole"
  ExternalGeometry = -> [Sketch027,Sketch]
  FullyConstrained = true
  MapMode = 5
  Placement = pos=(0,0,6) rot=(0,0,1;0rad)
  Support = -> [Hole011]
  sketch-geometry (3):
    g0: Circle CenterX=29.7366 CenterY=-75.5802 CenterZ=0 NormalX=0 NormalY=0 NormalZ=1 AngleXU=0 Radius=2.5
    g1: LineSegment StartX=-0.583397 StartY=-91.8945 StartZ=0 EndX=60.0566 EndY=-91.8945 EndZ=0
    g2: GeomPoint X=29.7366 Y=-91.8945 Z=0
  constraints (6):
    c: Radius(g0) = 2.5
    c: DistanceY(g-4,g0) = 25
    c: Coincident(g1,g-5)
    c: Coincident(g1,g-3)
    c: Symmetric(g1,g1,g2)
    c: Vertical(g2,g0)
FEATURE [PartDesign::Hole] Hole012
  BaseFeature = -> Hole011
  Depth = 25
  DepthType = 0
  Diameter = 4.2
  DrillForDepth = false
  DrillPoint = 1
  DrillPointAngle = 118
  HoleCutCountersinkAngle = 90
  HoleCutCustomValues = false
  HoleCutDepth = 0
  HoleCutDiameter = 6.1
  HoleCutType = 0
  ModelActualThread = false
  Profile = -> Sketch032
  Tapered = false
  TaperedAngle = 90
  ThreadAngle = 60
  ThreadClass = 0
  ThreadCutOffInner = 0.0866025
  ThreadCutOffOuter = 0.173205
  ThreadDirection = 0
  ThreadFit = 0
  ThreadPitch = 0.8
  ThreadSize = 13
  ThreadType = 1
  Threaded = true
FEATURE [Sketcher::SketchObject] Sketch033  label="y-plate-x-axis-cable-hole"
  ExternalGeometry = -> [Sketch025]
  FullyConstrained = true
  MapMode = 5
  Placement = pos=(0,0,6) rot=(0,0,1;0rad)
  Support = -> [Hole012]
  sketch-geometry (3):
    g0: Circle CenterX=-23.5834 CenterY=-16.7445 CenterZ=0 NormalX=0 NormalY=0 NormalZ=1 AngleXU=0 Radius=4.21
    g1: LineSegment StartX=-43.5834 StartY=-6.74454 StartZ=0 EndX=-43.5834 EndY=-26.7445 EndZ=0
    g2: GeomPoint X=-43.5834 Y=-16.7445 Z=0
  constraints (6):
    c: Radius(g0) = 4.21
    c: Coincident(g1,g-3)
    c: Coincident(g1,g-4)
    c: Symmetric(g1,g1,g2)
    c: Horizontal(g2,g0)
    c: DistanceX(g2,g0) = 20
FEATURE [PartDesign::Pocket] Pocket  label="po-y-plate-x-axis-cable-hole"
  BaseFeature = -> Hole012
  Length = 5
  Length2 = 100
  Profile = -> Sketch033
  Type = 1
COMPONENT P8 — recipe-attached ("X-Axis Left Plate", modeled in this document).
Construction recipe (the document's own serialized feature program — sketch geometry with constraints, then the solid features built on it; lengths are millimeters unless a unit is written):

FEATURE [PartDesign::Body] Body013  label="X-Axis Left Plate"
  BaseFeature = -> Body012
  Group = -> [Clone004]
  Origin = -> Origin017
  Placement = pos=(0,283,181.7) rot=(0.57735,-0.57735,-0.57735;2.0944rad)
  Tip = -> Clone004
  expr: .Placement.Base.y = Spreadsheet.y_axis_pos
FEATURE [PartDesign::FeatureBase] Clone004
  BaseFeature = -> Body012
COMPONENT P9 — recipe-attached ("X-Axis Right Plate", modeled in this document).
Construction recipe (the document's own serialized feature program — sketch geometry with constraints, then the solid features built on it; lengths are millimeters unless a unit is written):

FEATURE [PartDesign::Body] Body014  label="X-Axis Right Plate"
  BaseFeature = -> Body013
  Group = -> [Clone005]
  Origin = -> Origin018
  Placement = pos=(1000,586.4,0) rot=(0,0,1;3.14159rad)
  Tip = -> Clone005
  expr: .Placement.Base.y = Spreadsheet.y_axis_pos + 303.4
FEATURE [PartDesign::FeatureBase] Clone005
  BaseFeature = -> Body013
  Placement = pos=(-6,303.6,181.7) rot=(0.57735,0.57735,0.57735;2.0944rad)
COMPONENT P10 — recipe-attached ("Right Nema 17 Stepper Motor", modeled in this document).
Construction recipe (the document's own serialized feature program — sketch geometry with constraints, then the solid features built on it; lengths are millimeters unless a unit is written):

FEATURE [PartDesign::FeatureBase] Clone006
  BaseFeature = -> Part__Feature127
  Placement = pos=(-6,333.3,165.8) rot=(0,1,0;1.5708rad)
FEATURE [PartDesign::Body] Body015  label="Right Nema 17 Stepper Motor"
  BaseFeature = -> Part__Feature127
  Group = -> [Clone006]
  Origin = -> Origin019
  Placement = pos=(1000,586.4,0) rot=(0,0,1;3.14159rad)
  Tip = -> Clone006
  expr: .Placement.Base.y = Spreadsheet.y_axis_pos + 303.4
COMPONENT P11 — geometry summary ("Boolean"; no construction recipe available for this part):
  bounding box: 195.0 x 144.0 x 16.0 mm
  tessellated surface: 4,056 triangles
  volume: 56603 mm^3 (13% of its bounding box)
COMPONENT P12 — recipe-attached ("Head001", modeled in this document).
Construction recipe (the document's own serialized feature program — sketch geometry with constraints, then the solid features built on it; lengths are millimeters unless a unit is written):

FEATURE [PartDesign::SubShapeBinder] Binder003
  BindMode = 0
  ClaimChildren = false
  Context = -> Part001 [Body018.Binder003.]
  Fuse = false
  MakeFace = true
  PartialLoad = false
  Relative = true
  Support = -> [Body019[Hole026.]]
  _Version = 2
FEATURE [PartDesign::SubShapeBinder] Binder004
  BindMode = 0
  ClaimChildren = false
  Context = -> Part001 [Body018.Binder004.]
  Fuse = false
  MakeFace = true
  PartialLoad = false
  Relative = true
  Support = -> [Body019[Hole027.]]
  _Version = 2
FEATURE [PartDesign::SubShapeBinder] Binder
  BindMode = 0
  ClaimChildren = false
  Context = -> Part001 [Body018.Binder.]
  Fuse = false
  MakeFace = true
  PartialLoad = false
  Relative = true
  Support = -> [Body019[Hole031.]]
  _Version = 2
FEATURE [PartDesign::Body] Body018  label="Head Back"
  Group = -> [Sketch047,Sketch048,Sketch049,Sketch050,Binder003,Binder004,Sketch060,Pad010,Hole028,Pocket006,Hole029,Hole030,Sketch063,Binder,Hole032]
  Origin = -> Origin024
  Tip = -> Hole032
FEATURE [PartDesign::Body] Body019  label="Head Front"
  Group = -> [Sketch051,Sketch052,Sketch054,Sketch056,Sketch057,Sketch058,Sketch059,Pad009,Hole023,Pocket005,Hole024,Hole025,Hole026,Hole027,Sketch062,Hole031]
  Origin = -> Origin025
  Placement = pos=(0,0,40) rot=(0,0,1;0rad)
  Tip = -> Hole031
FEATURE [Sketcher::SketchObject] Sketch047  label="head-back-nema-mount-holes"
  FullyConstrained = true
  MapMode = 5
  Placement = pos=(0,0,6) rot=(0,0,1;0rad)
  Support = -> [Pad010]
  sketch-geometry (6):
    g0: Circle CenterX=-15.5 CenterY=-16 CenterZ=0 NormalX=0 NormalY=0 NormalZ=1 AngleXU=0 Radius=1.5
    g1: Circle CenterX=-15.5 CenterY=-47 CenterZ=0 NormalX=0 NormalY=0 NormalZ=1 AngleXU=0 Radius=1.5
    g2: Circle CenterX=15.5 CenterY=-16 CenterZ=0 NormalX=0 NormalY=0 NormalZ=1 AngleXU=0 Radius=1.5
    g3: Circle CenterX=15.5 CenterY=-47 CenterZ=0 NormalX=0 NormalY=0 NormalZ=1 AngleXU=0 Radius=1.5
    g4: LineSegment StartX=-15.5 StartY=-16 StartZ=0 EndX=15.5 EndY=-47 EndZ=0
    g5: GeomPoint X=-1.1e-15 Y=-31.5 Z=0
  constraints (15):
    c: Radius(g0) = 1.5
    c: Equal(g0,g2)
    c: Equal(g2,g3)
    c: Equal(g3,g1)
    c: Horizontal(g0,g2)
    c: Horizontal(g1,g3)
    c: Vertical(g0,g1)
    c: Vertical(g2,g3)
    c: DistanceX(g0,g2) = 31
    c: DistanceY(g1,g0) = 31
    c: Coincident(g4,g0)
    c: Coincident(g4,g3)
    c: Symmetric(g4,g4,g5)
    c: Vertical(g5,g-1)
    c: DistanceY(g5,g-1) = 31.5
FEATURE [Sketcher::SketchObject] Sketch048  label="head-back-excentric-wheel-holes"
  ExternalGeometry = -> [Binder003]
  FullyConstrained = false
  MapMode = 5
  Placement = pos=(0,0,6) rot=(0,0,1;0rad)
  Support = -> [Pocket006]
  sketch-geometry (2):
    g0: Circle CenterX=31 CenterY=-47 CenterZ=0 NormalX=0 NormalY=0 NormalZ=1 AngleXU=0 Radius=2.80181
    g1: Circle CenterX=-31 CenterY=-47 CenterZ=0 NormalX=0 NormalY=0 NormalZ=1 AngleXU=0 Radius=2.80181
  constraints (1):
    c: Equal(g1,g0)
FEATURE [Sketcher::SketchObject] Sketch049  label="head-back-wheel-holes"
  ExternalGeometry = -> [Sketch048,Binder004]
  FullyConstrained = true
  MapMode = 5
  Placement = pos=(0,0,6) rot=(0,0,1;0rad)
  Support = -> [Hole029]
  sketch-geometry (2):
    g0: Circle CenterX=-31 CenterY=-107 CenterZ=0 NormalX=0 NormalY=0 NormalZ=1 AngleXU=0 Radius=2.65
    g1: Circle CenterX=31 CenterY=-107 CenterZ=0 NormalX=0 NormalY=0 NormalZ=1 AngleXU=0 Radius=2.65
  constraints (4):
    c: Equal(g-5,g0)
    c: Equal(g0,g1)
    c: Coincident(g0,g-5)
    c: Coincident(g1,g-6)
FEATURE [Sketcher::SketchObject] Sketch050  label="head-back-nema-central-holes"
  ExternalGeometry = -> [Sketch047]
  FullyConstrained = false
  MapMode = 5
  Placement = pos=(0,0,6) rot=(0,0,1;0rad)
  Support = -> [Hole028]
  sketch-geometry (3):
    g0: LineSegment StartX=-15.5 StartY=-16 StartZ=0 EndX=15.5 EndY=-47 EndZ=0
    g1: GeomPoint X=9e-16 Y=-31.5 Z=0
    g2: Circle CenterX=9e-16 CenterY=-31.5 CenterZ=0 NormalX=0 NormalY=0 NormalZ=1 AngleXU=0 Radius=12.5
  constraints (3):
    c: Symmetric(g0,g0,g1)
    c: Coincident(g2,g1)
    c: Radius(g2) = 12.5
FEATURE [Sketcher::SketchObject] Sketch051  label="head-front-nema-mount-holes"
  FullyConstrained = true
  MapMode = 5
  Placement = pos=(0,0,6) rot=(0,0,1;0rad)
  Support = -> [Pad009]
  sketch-geometry (6):
    g0: Circle CenterX=-15.5 CenterY=15.5 CenterZ=0 NormalX=0 NormalY=0 NormalZ=1 AngleXU=0 Radius=2.5
    g1: Circle CenterX=15.5 CenterY=15.5 CenterZ=0 NormalX=0 NormalY=0 NormalZ=1 AngleXU=0 Radius=2.5
    g2: Circle CenterX=-15.5 CenterY=-15.5 CenterZ=0 NormalX=0 NormalY=0 NormalZ=1 AngleXU=0 Radius=2.5
    g3: Circle CenterX=15.5 CenterY=-15.5 CenterZ=0 NormalX=0 NormalY=0 NormalZ=1 AngleXU=0 Radius=2.5
    g4: LineSegment StartX=-15.5 StartY=15.5 StartZ=0 EndX=15.5 EndY=-15.5 EndZ=0
    g5: GeomPoint X=-1e-16 Y=-1e-16 Z=0
  constraints (14):
    c: Radius(g0) = 2.5
    c: Equal(g0,g1)
    c: Equal(g1,g3)
    c: Equal(g3,g2)
    c: Vertical(g0,g2)
    c: Vertical(g1,g3)
    c: Horizontal(g0,g1)
    c: Horizontal(g2,g3)
    c: DistanceX(g0,g1) = 31
    c: DistanceY(g3,g1) = 31
    c: Coincident(g4,g0)
    c: Coincident(g4,g3)
    c: Symmetric(g4,g4,g5)
    c: Coincident(g5,g-1)
FEATURE [Sketcher::SketchObject] Sketch052  label="head-front-nema-central-holes"
  ExternalGeometry = -> [Sketch051]
  FullyConstrained = true
  MapMode = 5
  Placement = pos=(0,0,6) rot=(0,0,1;0rad)
  Support = -> [Hole023]
  sketch-geometry (3):
    g0: LineSegment StartX=-15.5 StartY=15.5 StartZ=0 EndX=15.5 EndY=-15.5 EndZ=0
    g1: GeomPoint X=-4e-16 Y=4e-16 Z=0
    g2: Circle CenterX=-4e-16 CenterY=4e-16 CenterZ=0 NormalX=0 NormalY=0 NormalZ=1 AngleXU=0 Radius=12.5
  constraints (5):
    c: Coincident(g0,g-3)
    c: Coincident(g0,g-4)
    c: Symmetric(g0,g0,g1)
    c: Coincident(g2,g1)
    c: Radius(g2) = 12.5
FEATURE [Sketcher::SketchObject] Sketch054  label="head-front-nozzle-lift-transmission-pulley"
  ExternalGeometry = -> [Sketch057]
  FullyConstrained = true
  MapMode = 5
  Placement = pos=(0,0,6) rot=(0,0,1;0rad)
  Support = -> [Hole024]
  sketch-geometry (1):
    g0: Circle CenterX=0 CenterY=-129 CenterZ=0 NormalX=0 NormalY=0 NormalZ=1 AngleXU=0 Radius=1.5
  constraints (3):
    c: Radius(g0) = 1.5
    c: Vertical(g0,g-1)
    c: DistanceY(g0,g-3) = 16
FEATURE [Sketcher::SketchObject] Sketch056  label="head-front-wheel-holes"
  ExternalGeometry = -> [Sketch058]
  FullyConstrained = false
  MapMode = 5
  Placement = pos=(0,0,6) rot=(0,0,1;0rad)
  Support = -> [Hole026]
  sketch-geometry (3):
    g0: Circle CenterX=-31 CenterY=-107 CenterZ=0 NormalX=0 NormalY=0 NormalZ=1 AngleXU=0 Radius=2.5
    g1: Circle CenterX=31 CenterY=-107 CenterZ=0 NormalX=0 NormalY=0 NormalZ=1 AngleXU=0 Radius=2.5
    g2: Circle CenterX=-31 CenterY=-107 CenterZ=0 NormalX=0 NormalY=0 NormalZ=1 AngleXU=0 Radius=5.975
  constraints (6):
    c: Horizontal(g0,g1)
    c: Vertical(g-3,g0)
    c: Vertical(g-4,g1)
    c: DistanceY(g0,g-3) = 60
    c: Coincident(g2,g0)
    c: Radius(g2) = 5.975
FEATURE [Sketcher::SketchObject] Sketch057  label="head-front-hiwin-rails-mount-holes"
  FullyConstrained = false
  MapMode = 5
  Placement = pos=(0,0,6) rot=(0,0,1;0rad)
  Support = -> [Pocket005]
  sketch-geometry (11):
    g0: Circle CenterX=-13 CenterY=-53 CenterZ=0 NormalX=0 NormalY=0 NormalZ=1 AngleXU=0 Radius=1.5
    g1: Circle CenterX=-13 CenterY=-73 CenterZ=0 NormalX=0 NormalY=0 NormalZ=1 AngleXU=0 Radius=1.5
    g2: Circle CenterX=-13 CenterY=-93 CenterZ=0 NormalX=0 NormalY=0 NormalZ=1 AngleXU=0 Radius=1.5
    g3: Circle CenterX=-13 CenterY=-113 CenterZ=0 NormalX=0 NormalY=0 NormalZ=1 AngleXU=0 Radius=1.5
    g4: Circle CenterX=13 CenterY=-53 CenterZ=0 NormalX=0 NormalY=0 NormalZ=1 AngleXU=0 Radius=1.5
    g5: Circle CenterX=13 CenterY=-73 CenterZ=0 NormalX=0 NormalY=0 NormalZ=1 AngleXU=0 Radius=1.5
    g6: Circle CenterX=13 CenterY=-93 CenterZ=0 NormalX=0 NormalY=0 NormalZ=1 AngleXU=0 Radius=1.5
    g7: Circle CenterX=13 CenterY=-113 CenterZ=0 NormalX=0 NormalY=0 NormalZ=1 AngleXU=0 Radius=1.5
    g8: LineSegment StartX=-13 StartY=-53 StartZ=0 EndX=13 EndY=-53 EndZ=0
    g9: GeomPoint X=-2.864e-13 Y=-53 Z=0
    g10: LineSegment StartX=-17.5 StartY=-32.6577 StartZ=0 EndX=-17.5 EndY=-70.9981 EndZ=0
  constraints (29):
    c: Equal(g0,g1)
    c: Equal(g1,g2)
    c: Equal(g2,g3)
    c: Equal(g3,g4)
    c: Equal(g4,g5)
    c: Equal(g5,g6)
    c: Equal(g6,g7)
    c: Radius(g0) = 1.5
    c: Horizontal(g0,g4)
    c: Horizontal(g1,g5)
    c: Horizontal(g2,g6)
    c: Horizontal(g3,g7)
    c: Vertical(g4,g5)
    c: Vertical(g5,g6)
    c: Vertical(g6,g7)
    c: Vertical(g3,g2)
    c: Vertical(g2,g1)
    c: Vertical(g1,g0)
    c: DistanceX(g0,g4) = 26
    c: DistanceY(g1,g0) = 20
    c: DistanceY(g3,g2) = 20
    c: DistanceY(g2,g1) = 20
    c: Coincident(g8,g0)
    c: Coincident(g8,g4)
    c: Symmetric(g8,g8,g9)
    c: Vertical(g9,g-1)
    c: DistanceY(g7,g-1) = 113
    c: Vertical(g10)
    c: DistanceX(g10,g0) = 4.5
FEATURE [Sketcher::SketchObject] Sketch058  label="head-front-excentric-wheel-holes"
  FullyConstrained = true
  MapMode = 5
  Placement = pos=(0,0,6) rot=(0,0,1;0rad)
  Support = -> [Hole025]
  sketch-geometry (2):
    g0: Circle CenterX=-31 CenterY=-47 CenterZ=0 NormalX=0 NormalY=0 NormalZ=1 AngleXU=0 Radius=2.5
    g1: Circle CenterX=31 CenterY=-47 CenterZ=0 NormalX=0 NormalY=0 NormalZ=1 AngleXU=0 Radius=2.5
  constraints (6):
    c: Radius(g0) = 2.5
    c: Horizontal(g0,g1)
    c: Equal(g0,g1)
    c: DistanceX(g0,g-1) = 31
    c: DistanceX(g-1,g1) = 31
    c: DistanceY(g0,g-1) = 47
FEATURE [Sketcher::SketchObject] Sketch059  label="head-front-body"
  ExternalGeometry = -> [Sketch058,Sketch054]
  FullyConstrained = true
  MapMode = 5
  Support = -> [XY_Plane025]
  sketch-geometry (8):
    g0: LineSegment StartX=-38 StartY=22 StartZ=0 EndX=38 EndY=22 EndZ=0
    g1: LineSegment StartX=41 StartY=19 StartZ=0 EndX=41 EndY=-136 EndZ=0
    g2: LineSegment StartX=38 StartY=-139 StartZ=0 EndX=-38 EndY=-139 EndZ=0
    g3: LineSegment StartX=-41 StartY=-136 StartZ=0 EndX=-41 EndY=19 EndZ=0
    g4: ArcOfCircle CenterX=-38 CenterY=19 CenterZ=0 NormalX=0 NormalY=0 NormalZ=1 AngleXU=0 Radius=3 StartAngle=1.5708 EndAngle=3.14159
    g5: ArcOfCircle CenterX=38 CenterY=19 CenterZ=0 NormalX=0 NormalY=0 NormalZ=1 AngleXU=0 Radius=3 StartAngle=4.143e-13 EndAngle=1.5708
    g6: ArcOfCircle CenterX=38 CenterY=-136 CenterZ=0 NormalX=0 NormalY=0 NormalZ=1 AngleXU=0 Radius=3 StartAngle=4.71239 EndAngle=6.28319
    g7: ArcOfCircle CenterX=-38 CenterY=-136 CenterZ=0 NormalX=0 NormalY=0 NormalZ=1 AngleXU=0 Radius=3 StartAngle=3.14159 EndAngle=4.71239
  constraints (20):
    c: Horizontal(g0)
    c: Horizontal(g2)
    c: Vertical(g1)
    c: Vertical(g3)
    c: Tangent(g0,g4) = 1.5708
    c: Tangent(g3,g4) = 1.5708
    c: Tangent(g0,g5) = 1.5708
    c: Tangent(g1,g5) = 1.5708
    c: Tangent(g1,g6) = 1.5708
    c: Tangent(g2,g6) = 1.5708
    c: Tangent(g2,g7) = 1.5708
    c: Tangent(g3,g7) = 1.5708
    c: Radius(g4) = 3
    c: Equal(g4,g5)
    c: Equal(g5,g6)
    c: Equal(g6,g7)
    c: DistanceX(g3,g-3) = 10
    c: DistanceX(g-5,g1) = 10
    c: DistanceY(g2,g-4) = 10
    c: DistanceY(g-1,g0) = 22
FEATURE [PartDesign::Pad] Pad009  label="pd-head-front-body"
  Direction = (1,1,1)
  Length = 6
  Length2 = 100
  Profile = -> Sketch059
  Type = 0
FEATURE [PartDesign::Hole] Hole023  label="ho-head-front-nema-mount-holes"
  BaseFeature = -> Pad009
  Depth = 25
  DepthType = 0
  Diameter = 3.2
  DrillForDepth = false
  DrillPoint = 1
  DrillPointAngle = 118
  HoleCutCountersinkAngle = 90
  HoleCutCustomValues = false
  HoleCutDepth = 0
  HoleCutDiameter = 6.1
  HoleCutType = 0
  ModelActualThread = false
  Profile = -> Sketch051
  Tapered = false
  TaperedAngle = 90
  ThreadAngle = 0
  ThreadClass = 0
  ThreadCutOffInner = 0
  ThreadCutOffOuter = 0
  ThreadDirection = 0
  ThreadFit = 1
  ThreadPitch = 0
  ThreadSize = 9
  ThreadType = 1
  Threaded = false
FEATURE [PartDesign::Pocket] Pocket005  label="po-head-front-nema-central-holes"
  BaseFeature = -> Hole023
  Length = 5
  Length2 = 100
  Profile = -> Sketch052
  Type = 1
FEATURE [PartDesign::Hole] Hole024  label="ho-head-front-hiwin-rails-mount-holes"
  BaseFeature = -> Pocket005
  Depth = 25
  DepthType = 0
  Diameter = 2.5
  DrillForDepth = false
  DrillPoint = 1
  DrillPointAngle = 118
  HoleCutCountersinkAngle = 90
  HoleCutCustomValues = false
  HoleCutDepth = 0
  HoleCutDiameter = 6.1
  HoleCutType = 0
  ModelActualThread = false
  Profile = -> Sketch057
  Tapered = false
  TaperedAngle = 90
  ThreadAngle = 60
  ThreadClass = 0
  ThreadCutOffInner = 0.0541266
  ThreadCutOffOuter = 0.108253
  ThreadDirection = 0
  ThreadFit = 1
  ThreadPitch = 0.5
  ThreadSize = 9
  ThreadType = 1
  Threaded = true
FEATURE [PartDesign::Hole] Hole025  label="ho-head-front-nozzle-lift-transmission-pulley"
  BaseFeature = -> Hole024
  Depth = 25
  DepthType = 0
  Diameter = 2.5
  DrillForDepth = false
  DrillPoint = 1
  DrillPointAngle = 118
  HoleCutCountersinkAngle = 90
  HoleCutCustomValues = false
  HoleCutDepth = 0
  HoleCutDiameter = 6.1
  HoleCutType = 0
  ModelActualThread = false
  Profile = -> Sketch054
  Tapered = false
  TaperedAngle = 90
  ThreadAngle = 60
  ThreadClass = 0
  ThreadCutOffInner = 0.0541266
  ThreadCutOffOuter = 0.108253
  ThreadDirection = 0
  ThreadFit = 1
  ThreadPitch = 0.5
  ThreadSize = 9
  ThreadType = 1
  Threaded = true
FEATURE [PartDesign::Hole] Hole026  label="ho-head-front-excentric-wheel-holes"
  BaseFeature = -> Hole025
  Depth = 25
  DepthType = 0
  Diameter = 7.2
  DrillForDepth = false
  DrillPoint = 1
  DrillPointAngle = 118
  HoleCutCountersinkAngle = 90
  HoleCutCustomValues = false
  HoleCutDepth = 0
  HoleCutDiameter = 6.1
  HoleCutType = 0
  ModelActualThread = false
  Profile = -> Sketch058
  Tapered = false
  TaperedAngle = 90
  ThreadAngle = 0
  ThreadClass = 0
  ThreadCutOffInner = 0
  ThreadCutOffOuter = 0
  ThreadDirection = 0
  ThreadFit = 0
  ThreadPitch = 0
  ThreadSize = 0
  ThreadType = 0
  Threaded = false
FEATURE [PartDesign::Hole] Hole027  label="ho-head-front-wheel-holes"
  BaseFeature = -> Hole026
  Depth = 25
  DepthType = 0
  Diameter = 5.3
  DrillForDepth = false
  DrillPoint = 1
  DrillPointAngle = 118
  HoleCutCountersinkAngle = 90
  HoleCutCustomValues = false
  HoleCutDepth = 0
  HoleCutDiameter = 6.1
  HoleCutType = 0
  ModelActualThread = false
  Profile = -> Sketch056
  Tapered = false
  TaperedAngle = 90
  ThreadAngle = 0
  ThreadClass = 0
  ThreadCutOffInner = 0
  ThreadCutOffOuter = 0
  ThreadDirection = 0
  ThreadFit = 1
  ThreadPitch = 0
  ThreadSize = 13
  ThreadType = 1
  Threaded = false
FEATURE [Sketcher::SketchObject] Sketch060  label="head-back-body"
  ExternalGeometry = -> [Sketch049,Binder003]
  FullyConstrained = false
  MapMode = 5
  Support = -> [XY_Plane024]
  sketch-geometry (8):
    g0: LineSegment StartX=-38 StartY=-8.9852 StartZ=0 EndX=38 EndY=-8.9852 EndZ=0
    g1: LineSegment StartX=41 StartY=-11.9852 StartZ=0 EndX=41 EndY=-119 EndZ=0
    g2: LineSegment StartX=38 StartY=-122 StartZ=0 EndX=-38 EndY=-122 EndZ=0
    g3: LineSegment StartX=-41 StartY=-119 StartZ=0 EndX=-41 EndY=-11.9852 EndZ=0
    g4: ArcOfCircle CenterX=-38 CenterY=-11.9852 CenterZ=0 NormalX=0 NormalY=0 NormalZ=1 AngleXU=0 Radius=3 StartAngle=1.5708 EndAngle=3.14159
    g5: ArcOfCircle CenterX=-38 CenterY=-119 CenterZ=0 NormalX=0 NormalY=0 NormalZ=1 AngleXU=0 Radius=3 StartAngle=3.14159 EndAngle=4.71239
    g6: ArcOfCircle CenterX=38 CenterY=-119 CenterZ=0 NormalX=0 NormalY=0 NormalZ=1 AngleXU=0 Radius=3 StartAngle=4.71239 EndAngle=6.28319
    g7: ArcOfCircle CenterX=38 CenterY=-11.9852 CenterZ=0 NormalX=0 NormalY=0 NormalZ=1 AngleXU=0 Radius=3 StartAngle=7.652e-13 EndAngle=1.5708
  constraints (19):
    c: Horizontal(g0)
    c: Horizontal(g2)
    c: Vertical(g1)
    c: Vertical(g3)
    c: Tangent(g0,g4) = 1.5708
    c: Tangent(g3,g4) = 1.5708
    c: Tangent(g2,g5) = 1.5708
    c: Tangent(g3,g5) = 1.5708
    c: Tangent(g1,g6) = 1.5708
    c: Tangent(g2,g6) = 1.5708
    c: Tangent(g0,g7) = 1.5708
    c: Tangent(g1,g7) = 1.5708
    c: Radius(g4) = 3
    c: Equal(g4,g7)
    c: Equal(g7,g6)
    c: Equal(g6,g5)
    c: DistanceY(g2,g-3) = 15
    c: Vertical(g3,g-4)
    c: Vertical(g1,g-5)
FEATURE [PartDesign::Pad] Pad010  label="pd-head-back-body"
  Direction = (1,1,1)
  Length = 6
  Length2 = 100
  Profile = -> Sketch060
  Type = 0
FEATURE [PartDesign::Hole] Hole028  label="ho-head-back-nema-mount-holes"
  BaseFeature = -> Pad010
  Depth = 25
  DepthType = 0
  Diameter = 3.2
  DrillForDepth = false
  DrillPoint = 1
  DrillPointAngle = 118
  HoleCutCountersinkAngle = 90
  HoleCutCustomValues = false
  HoleCutDepth = 0
  HoleCutDiameter = 6.1
  HoleCutType = 0
  ModelActualThread = false
  Profile = -> Sketch047
  Tapered = false
  TaperedAngle = 90
  ThreadAngle = 0
  ThreadClass = 0
  ThreadCutOffInner = 0
  ThreadCutOffOuter = 0
  ThreadDirection = 0
  ThreadFit = 1
  ThreadPitch = 0
  ThreadSize = 9
  ThreadType = 1
  Threaded = false
FEATURE [PartDesign::Pocket] Pocket006  label="po-head-back-nema-central-holes"
  BaseFeature = -> Hole028
  Length = 5
  Length2 = 100
  Profile = -> Sketch050
  Type = 1
FEATURE [PartDesign::Hole] Hole029  label="ho-head-back-excentric-wheel-holes"
  BaseFeature = -> Pocket006
  Depth = 25
  DepthType = 0
  Diameter = 7.2
  DrillForDepth = false
  DrillPoint = 1
  DrillPointAngle = 118
  HoleCutCountersinkAngle = 90
  HoleCutCustomValues = false
  HoleCutDepth = 0
  HoleCutDiameter = 0
  HoleCutType = 0
  ModelActualThread = false
  Profile = -> Sketch048
  Tapered = false
  TaperedAngle = 90
  ThreadAngle = 0
  ThreadClass = 0
  ThreadCutOffInner = 0
  ThreadCutOffOuter = 0
  ThreadDirection = 0
  ThreadFit = 0
  ThreadPitch = 0
  ThreadSize = 0
  ThreadType = 0
  Threaded = false
FEATURE [PartDesign::Hole] Hole030  label="ho-head-back-wheel-holes"
  BaseFeature = -> Hole029
  Depth = 25
  DepthType = 0
  Diameter = 5.3
  DrillForDepth = false
  DrillPoint = 1
  DrillPointAngle = 118
  HoleCutCountersinkAngle = 90
  HoleCutCustomValues = false
  HoleCutDepth = 0
  HoleCutDiameter = 6.1
  HoleCutType = 0
  ModelActualThread = false
  Profile = -> Sketch049
  Tapered = false
  TaperedAngle = 90
  ThreadAngle = 0
  ThreadClass = 0
  ThreadCutOffInner = 0
  ThreadCutOffOuter = 0
  ThreadDirection = 0
  ThreadFit = 1
  ThreadPitch = 0
  ThreadSize = 13
  ThreadType = 1
  Threaded = false
FEATURE [Sketcher::SketchObject] Sketch062  label="head-front-camera-fix-holes"
  ExternalGeometry = -> [Sketch056,Sketch057]
  FullyConstrained = false
  MapMode = 5
  Placement = pos=(0,0,6) rot=(0,0,1;0rad)
  Support = -> [Hole027]
  sketch-geometry (17):
    g0: Circle CenterX=-31 CenterY=-107 CenterZ=0 NormalX=0 NormalY=0 NormalZ=1 AngleXU=0 Radius=5.975
    g1: Circle CenterX=31 CenterY=-107 CenterZ=0 NormalX=0 NormalY=0 NormalZ=1 AngleXU=0 Radius=5.975
    g2: LineSegment StartX=-17.5 StartY=-48.1779 StartZ=0 EndX=-8.5 EndY=-48.1779 EndZ=0
    g3: LineSegment StartX=-8.5 StartY=-48.1779 StartZ=0 EndX=-8.5 EndY=-126.353 EndZ=0
    g4: LineSegment StartX=-8.5 StartY=-126.353 StartZ=0 EndX=-17.5 EndY=-126.353 EndZ=0
    g5: LineSegment StartX=-17.5 StartY=-126.353 StartZ=0 EndX=-17.5 EndY=-48.1779 EndZ=0
    g6: GeomPoint X=-13 Y=-126.353 Z=0
    g7: LineSegment StartX=8.5 StartY=-48.1779 StartZ=0 EndX=17.5 EndY=-48.1779 EndZ=0
    g8: LineSegment StartX=17.5 StartY=-48.1779 StartZ=0 EndX=17.5 EndY=-126.353 EndZ=0
    g9: LineSegment StartX=17.5 StartY=-126.353 StartZ=0 EndX=8.5 EndY=-126.353 EndZ=0
    g10: LineSegment StartX=8.5 StartY=-126.353 StartZ=0 EndX=8.5 EndY=-48.1779 EndZ=0
    g11: GeomPoint X=13 Y=-126.353 Z=0
    g12: GeomPoint X=-25.025 Y=-107 Z=0
    g13: GeomPoint X=-31 Y=-101.025 Z=0
    g14: LineSegment StartX=-31 StartY=-101.025 StartZ=0 EndX=31 EndY=-101.025 EndZ=0
    g15: Circle CenterX=-23.5 CenterY=-117 CenterZ=0 NormalX=0 NormalY=0 NormalZ=1 AngleXU=0 Radius=1.5
    g16: Circle CenterX=23.5 CenterY=-117 CenterZ=0 NormalX=0 NormalY=0 NormalZ=1 AngleXU=0 Radius=1.5
  constraints (41):
    c: Coincident(g0,g-3)
    c: Radius(g0) = 5.975
    c: Coincident(g1,g-4)
    c: Equal(g0,g1)
    c: Coincident(g2,g3)
    c: Coincident(g3,g4)
    c: Coincident(g4,g5)
    c: Coincident(g5,g2)
    c: Horizontal(g2)
    c: Horizontal(g4)
    c: Vertical(g3)
    c: Vertical(g5)
    c: Symmetric(g4,g4,g6)
    c: Vertical(g6,g-5)
    c: DistanceX(g2,g2) = 9
    c: Coincident(g7,g8)
    c: Coincident(g8,g9)
    c: Coincident(g9,g10)
    c: Coincident(g10,g7)
    c: Horizontal(g7)
    c: Horizontal(g9)
    c: Vertical(g8)
    c: Vertical(g10)
    c: Symmetric(g9,g9,g11)
    c: Vertical(g11,g-6)
    c: Horizontal(g3,g9)
    c: Equal(g2,g7)
    c: Equal(g3,g8)
    c: PointOnObject(g12,g0)
    c: Horizontal(g0,g12)
    c: PointOnObject(g13,g0)
    c: Vertical(g13,g0)
    c: Coincident(g14,g13)
    c: PointOnObject(g14,g1)
    c: Horizontal(g14)
    c: Equal(g15,g16)
    c: Equal(g16,g-5)
    c: Horizontal(g15,g16)
    c: DistanceX(g15,g4) = 6
    c: DistanceX(g8,g16) = 6
    c: DistanceY(g15,g12) = 10
FEATURE [PartDesign::Hole] Hole031  label="ho-head-front-camera-fix-holes"
  BaseFeature = -> Hole027
  Depth = 25
  DepthType = 0
  Diameter = 3.2
  DrillForDepth = false
  DrillPoint = 1
  DrillPointAngle = 118
  HoleCutCountersinkAngle = 90
  HoleCutCustomValues = false
  HoleCutDepth = 0
  HoleCutDiameter = 6.1
  HoleCutType = 0
  ModelActualThread = false
  Profile = -> Sketch062
  Tapered = false
  TaperedAngle = 90
  ThreadAngle = 0
  ThreadClass = 0
  ThreadCutOffInner = 0
  ThreadCutOffOuter = 0
  ThreadDirection = 0
  ThreadFit = 1
  ThreadPitch = 0
  ThreadSize = 9
  ThreadType = 1
  Threaded = false
FEATURE [Sketcher::SketchObject] Sketch063  label="head-back-camera-fix-holes"
  ExternalGeometry = -> [Binder]
  FullyConstrained = true
  MapMode = 5
  Placement = pos=(0,0,6) rot=(0,0,1;0rad)
  Support = -> [Hole030]
  sketch-geometry (2):
    g0: Circle CenterX=-23.5 CenterY=-117 CenterZ=0 NormalX=0 NormalY=0 NormalZ=1 AngleXU=0 Radius=1.6
    g1: Circle CenterX=23.5 CenterY=-117 CenterZ=0 NormalX=0 NormalY=0 NormalZ=1 AngleXU=0 Radius=1.6
  constraints (4):
    c: Equal(g0,g1)
    c: Equal(g1,g-3)
    c: Coincident(g0,g-3)
    c: Coincident(g1,g-4)
FEATURE [PartDesign::Hole] Hole032  label="ho-head-back-camera-fix-holes"
  BaseFeature = -> Hole030
  Depth = 25
  DepthType = 0
  Diameter = 2.5
  DrillForDepth = false
  DrillPoint = 1
  DrillPointAngle = 118
  HoleCutCountersinkAngle = 90
  HoleCutCustomValues = false
  HoleCutDepth = 0
  HoleCutDiameter = 6.1
  HoleCutType = 0
  ModelActualThread = false
  Profile = -> Sketch063
  Tapered = false
  TaperedAngle = 90
  ThreadAngle = 60
  ThreadClass = 0
  ThreadCutOffInner = 0.0541266
  ThreadCutOffOuter = 0.108253
  ThreadDirection = 0
  ThreadFit = 1
  ThreadPitch = 0.5
  ThreadSize = 9
  ThreadType = 1
  Threaded = true
COMPONENT P13 — geometry summary ("24 V power supply"; no construction recipe available for this part):
  bounding box: 215.0 x 114.0 x 51.2 mm
  tessellated surface: 53,098 triangles
  volume: 203977 mm^3 (16% of its bounding box)
COMPONENT P14 — geometry summary ("12 V power supply"; no construction recipe available for this part):
  bounding box: 215.0 x 114.0 x 51.2 mm
  tessellated surface: 53,100 triangles
  volume: 203977 mm^3 (16% of its bounding box)
PROVENANCE & LICENSES
A FreeCAD (.FCStd) document from a public repository crawl; recipes are the document's own serialized feature recipes (and, for linked parts, companion documents' recipes).
License: gpl-3.0.
